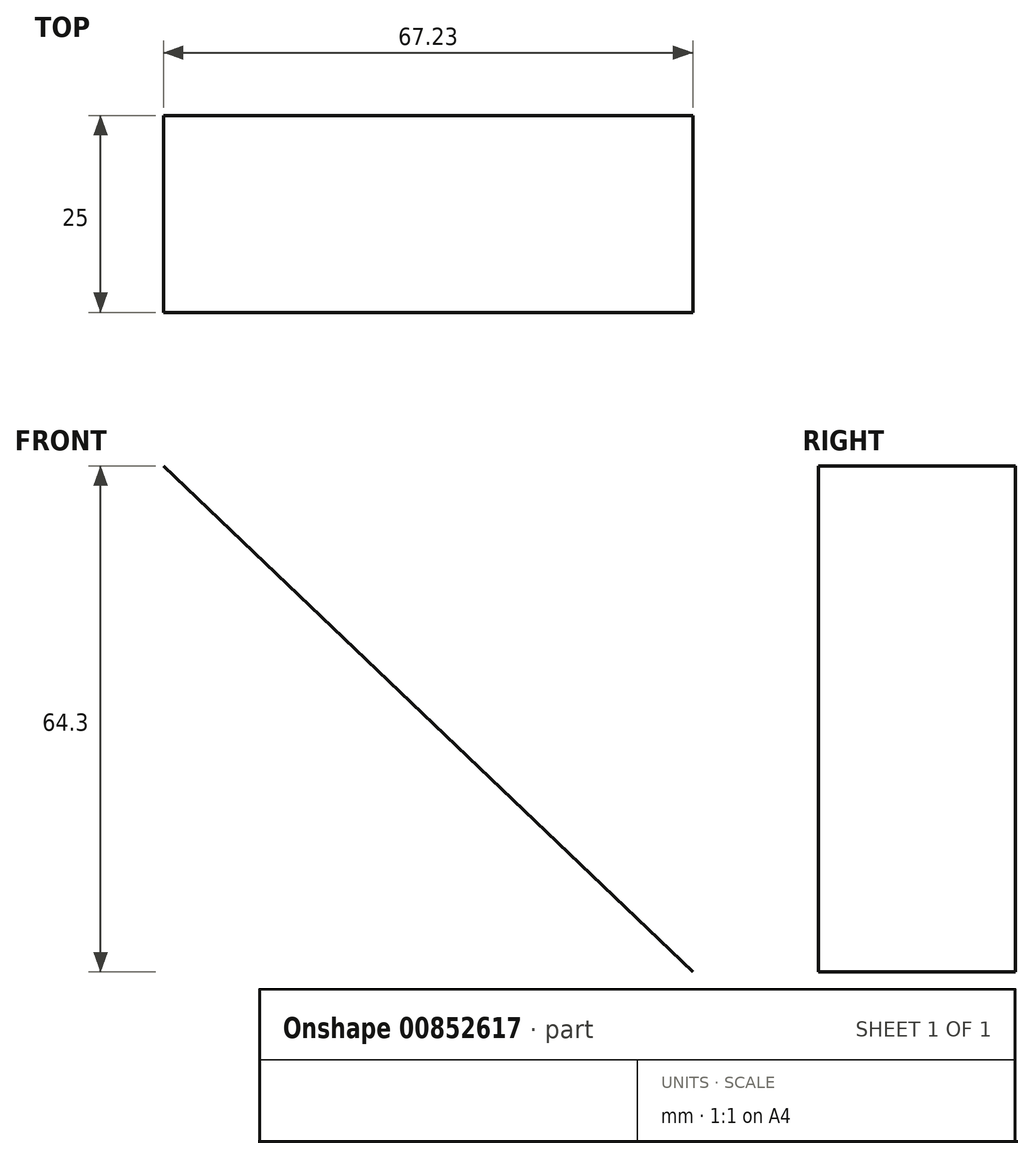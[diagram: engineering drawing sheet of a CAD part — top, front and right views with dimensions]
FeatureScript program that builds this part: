
annotation { "Feature Type Name" : "Feature", "Feature Type Description" : "" }
export const myFeature = defineFeature(function(context is Context, id is Id, definition is map)
    precondition{}
    {
        {
            var Q0;
            Q0=qCreatedBy(makeId("Front.planeOp"),FACE);
            var sketch = newSketch(context, id + "F0", { "sketchPlane" : qUnion([Q0])});
            skLineSegment(sketch, "E0", {"start": v(-137.66, 21.95) * mm, "end": v(-70.43, -42.35) * mm});
            skSolve(sketch);
        }
        {
            var Q0;
            Q0 = qSketchRegion(id + "F0", true);
            var Q1;
            Q1=sQuery(id+"F0.wireOp",EDGE,"E0");
            extrude(context, id + "F1", {"entities" : qUnion([Q0]), "bodyType" : ToolBodyType.SURFACE, "surfaceEntities" : qUnion([Q1]), "depth" : 25 * mm, "offsetDistance" : 25 * mm});
        }
    });
